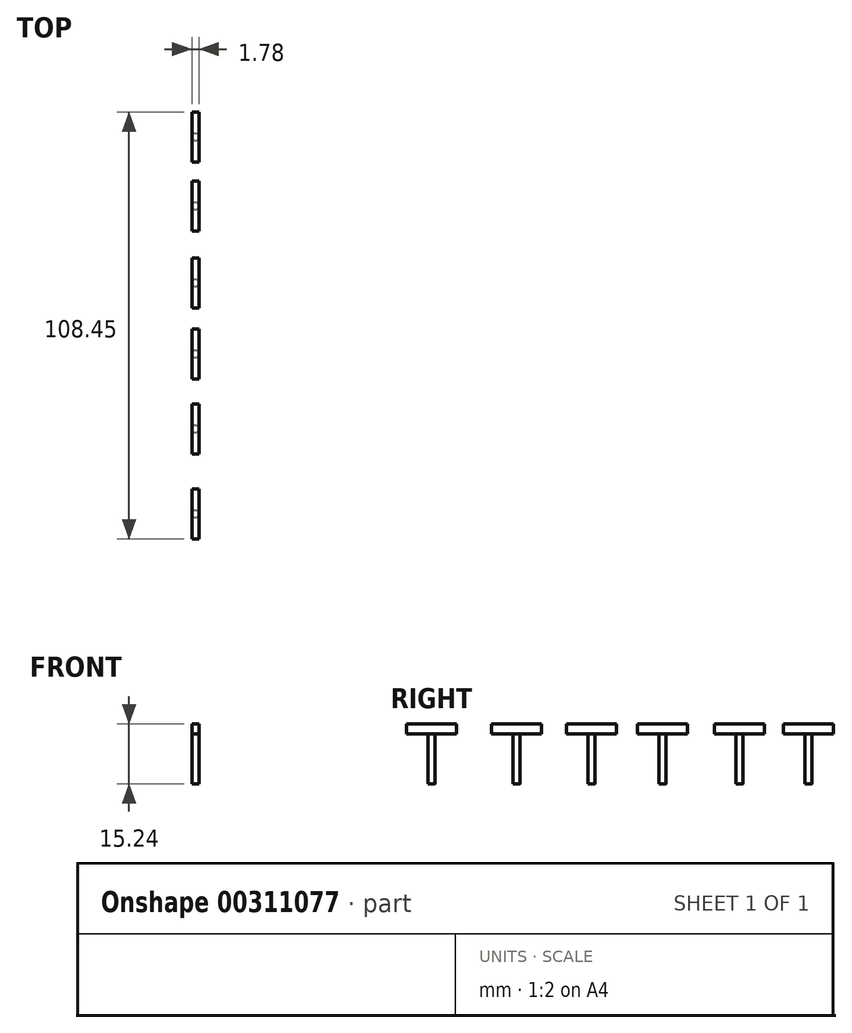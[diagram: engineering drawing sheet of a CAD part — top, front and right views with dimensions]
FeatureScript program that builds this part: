
annotation { "Feature Type Name" : "Feature", "Feature Type Description" : "" }
export const myFeature = defineFeature(function(context is Context, id is Id, definition is map)
    precondition{}
    {
        {
            var Q0;
            Q0=qCreatedBy(makeId("Top.planeOp"),FACE);
            var sketch = newSketch(context, id + "F0", { "sketchPlane" : qUnion([Q0])});
            skCircle(sketch, "E0", {"center": v(0, 0) * mm, "radius": 0.89 * mm});
            skSolve(sketch);
        }
        {
            var Q0;
            Q0=makeQuery(id+"F0.imprint","IMPRINT",FACE,{"disambiguationData":[TD([[makeQuery(id+"F0.imprint","IMPRINT",EDGE,{"derivedFrom":sQuery(id+"F0.wireOp",EDGE,"E0")}),1.0]])]});
            extrude(context, id + "F1", {"entities" : qUnion([Q0]), "oppositeDirection" : true, "depth" : 12.7 * mm});
        }
        {
            var Q0;
            Q0=qCreatedBy(makeId("Front.planeOp"),FACE);
            cPlane(context, id + "F2", {"entities" : qUnion([Q0]), "cplaneType" : CPlaneType.OFFSET, "offset" : 6.35 * mm, "width" : 152.4 * mm, "height" : 152.4 * mm});
        }
        {
            var Q0;
            Q0=qCreatedBy(id+"F2.planeOp",FACE);
            var sketch = newSketch(context, id + "F3", { "sketchPlane" : qUnion([Q0])});
            skLineSegment(sketch, "E1", {"start": v(0.89, 0) * mm, "end": v(0.89, 2.54) * mm});
            skLineSegment(sketch, "E2", {"start": v(0.89, 2.54) * mm, "end": v(-0.89, 2.54) * mm});
            skLineSegment(sketch, "E3", {"start": v(-0.89, 2.54) * mm, "end": v(-0.89, 0) * mm});
            skLineSegment(sketch, "E4", {"start": v(-0.89, 0) * mm, "end": v(0.89, 0) * mm});
            skSolve(sketch);
        }
        {
            var Q0;
            Q0=makeQuery(id+"F3.imprint","IMPRINT",FACE,{"disambiguationData":[TD([[makeQuery(id+"F3.imprint","IMPRINT",EDGE,{"derivedFrom":sQuery(id+"F3.wireOp",EDGE,"E1")}),1.0]])]});
            extrude(context, id + "F4", {"entities" : qUnion([Q0]), "operationType" : NewBodyOperationType.ADD, "oppositeDirection" : true, "depth" : 12.7 * mm});
        }
        {
            var Q0;
            Q0=makeQuery(id+"F1.opExtrude","SWEPT_BODY",BODY,{"disambiguationData":[OSD([sQuery(id+"F0.wireOp",EDGE,"E0")])]});
            transform(context, id + "F5", {"entities" : qUnion([Q0]), "transformType" : TransformType.TRANSLATION_3D, "dx" : 0 * mm, "dy" : 19.56 * mm, "dz" : 0 * mm, "makeCopy" : true});
        }
        {
            var Q0;
            Q0=makeQuery(id+"F5.opPattern","COPY",BODY,{"derivedFrom":makeQuery(id+"F1.opExtrude","SWEPT_BODY",BODY,{"disambiguationData":[OSD([sQuery(id+"F0.wireOp",EDGE,"E0")])]}),"instanceName":"1"});
            transform(context, id + "F6", {"entities" : qUnion([Q0]), "transformType" : TransformType.TRANSLATION_3D, "dx" : 0 * mm, "dy" : 17.53 * mm, "dz" : 0 * mm, "makeCopy" : true});
        }
        {
            var Q0;
            Q0=makeQuery(id+"F6.opPattern","COPY",BODY,{"derivedFrom":makeQuery(id+"F5.opPattern","COPY",BODY,{"derivedFrom":makeQuery(id+"F1.opExtrude","SWEPT_BODY",BODY,{"disambiguationData":[OSD([sQuery(id+"F0.wireOp",EDGE,"E0")])]}),"instanceName":"1"}),"instanceName":"1"});
            transform(context, id + "F7", {"entities" : qUnion([Q0]), "transformType" : TransformType.TRANSLATION_3D, "dx" : 0 * mm, "dy" : -55.12 * mm, "dz" : 0 * mm, "makeCopy" : true});
        }
        {
            var Q0;
            Q0=makeQuery(id+"F7.opPattern","COPY",BODY,{"derivedFrom":makeQuery(id+"F6.opPattern","COPY",BODY,{"derivedFrom":makeQuery(id+"F5.opPattern","COPY",BODY,{"derivedFrom":makeQuery(id+"F1.opExtrude","SWEPT_BODY",BODY,{"disambiguationData":[OSD([sQuery(id+"F0.wireOp",EDGE,"E0")])]}),"instanceName":"1"}),"instanceName":"1"}),"instanceName":"1"});
            transform(context, id + "F8", {"entities" : qUnion([Q0]), "transformType" : TransformType.TRANSLATION_3D, "dx" : 0 * mm, "dy" : -19.05 * mm, "dz" : 0 * mm, "makeCopy" : true});
        }
        {
            var Q0;
            Q0=makeQuery(id+"F8.opPattern","COPY",BODY,{"derivedFrom":makeQuery(id+"F7.opPattern","COPY",BODY,{"derivedFrom":makeQuery(id+"F6.opPattern","COPY",BODY,{"derivedFrom":makeQuery(id+"F5.opPattern","COPY",BODY,{"derivedFrom":makeQuery(id+"F1.opExtrude","SWEPT_BODY",BODY,{"disambiguationData":[OSD([sQuery(id+"F0.wireOp",EDGE,"E0")])]}),"instanceName":"1"}),"instanceName":"1"}),"instanceName":"1"}),"instanceName":"1"});
            transform(context, id + "F9", {"entities" : qUnion([Q0]), "transformType" : TransformType.TRANSLATION_3D, "dx" : 0 * mm, "dy" : -21.59 * mm, "dz" : 0 * mm, "makeCopy" : true});
        }
    });
